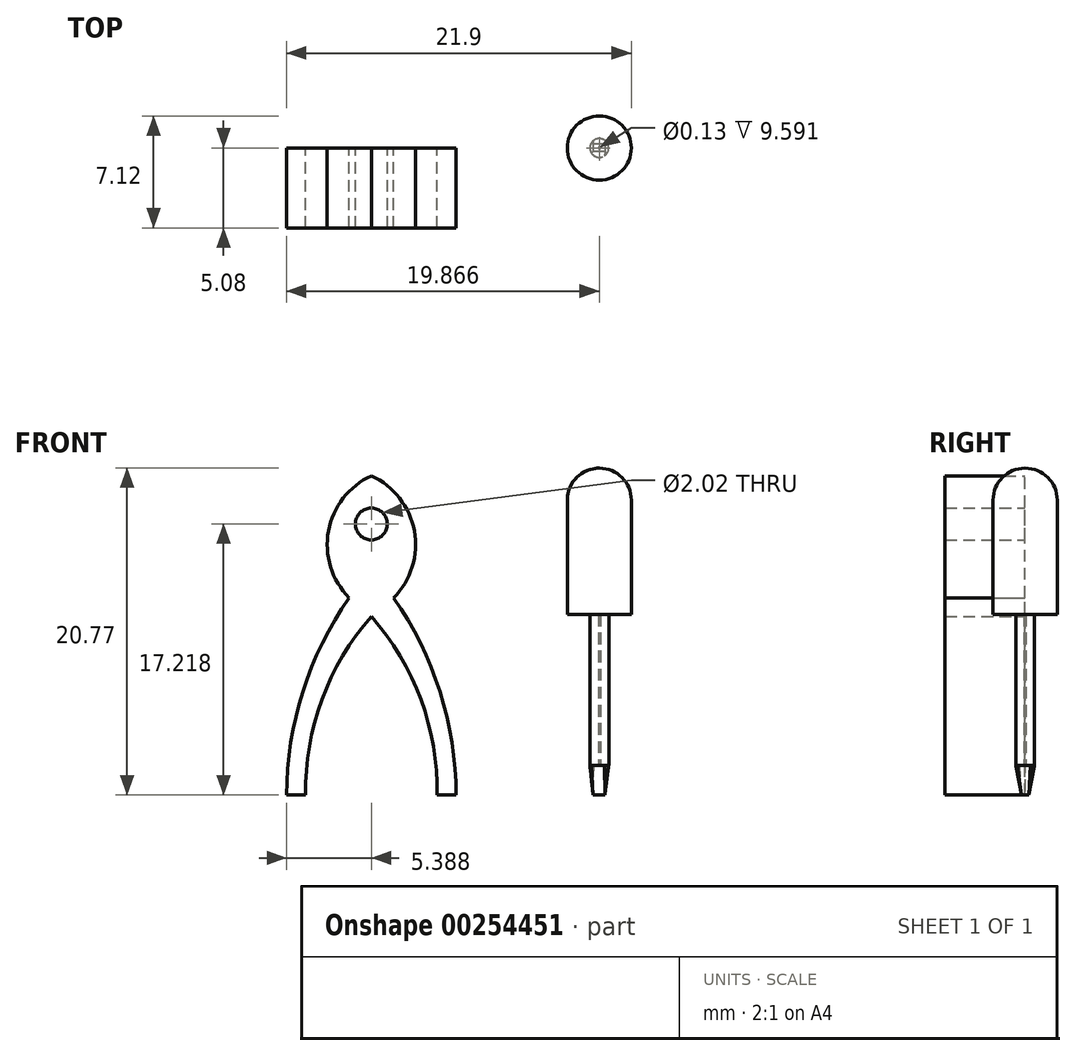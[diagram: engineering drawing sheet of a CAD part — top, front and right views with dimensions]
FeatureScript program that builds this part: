
annotation { "Feature Type Name" : "Feature", "Feature Type Description" : "" }
export const myFeature = defineFeature(function(context is Context, id is Id, definition is map)
    precondition{}
    {
        {
            var Q0;
            Q0=qCreatedBy(makeId("Front.planeOp"),FACE);
            var sketch = newSketch(context, id + "F0", { "sketchPlane" : qUnion([Q0])});
            skArc(sketch, "E0", {"start": v(5.39, 14.35) * mm, "mid": v(1.41, 7.66) * mm, "end": v(0, 0) * mm});
            skLineSegment(sketch, "E1", {"start": v(0, 0) * mm, "end": v(1.21, 0) * mm});
            skLineSegment(sketch, "E2", {"start": v(5.39, 14.35) * mm, "end": v(5.39, 11.35) * mm});
            skArc(sketch, "E3", {"start": v(5.39, 11.35) * mm, "mid": v(2.25, 6.06) * mm, "end": v(1.21, 0) * mm});
            skArc(sketch, "E4.MirrorCS", {"start": v(5.39, 14.35) * mm, "mid": v(9.37, 7.66) * mm, "end": v(10.78, 0) * mm});
            skArc(sketch, "E5.MirrorCS", {"start": v(5.39, 11.35) * mm, "mid": v(8.53, 6.06) * mm, "end": v(9.57, 0) * mm});
            skLineSegment(sketch, "E6.MirrorCS", {"start": v(10.78, 0) * mm, "end": v(9.57, 0) * mm});
            skArc(sketch, "E7", {"start": v(5.39, 20.28) * mm, "mid": v(2.66, 16.77) * mm, "end": v(3.97, 12.53) * mm});
            skLineSegment(sketch, "E8", {"start": v(5.39, 20.28) * mm, "end": v(5.39, 18.23) * mm});
            skLineSegment(sketch, "E9", {"start": v(5.39, 14.35) * mm, "end": v(5.39, 16.2) * mm});
            skArc(sketch, "E10", {"start": v(5.39, 18.23) * mm, "mid": v(4.38, 17.22) * mm, "end": v(5.39, 16.2) * mm});
            skArc(sketch, "E11.MirrorCS", {"start": v(5.39, 18.23) * mm, "mid": v(6.4, 17.22) * mm, "end": v(5.39, 16.2) * mm});
            skArc(sketch, "E12.MirrorCS", {"start": v(5.39, 20.28) * mm, "mid": v(8.11, 16.77) * mm, "end": v(6.8, 12.53) * mm});
            skSolve(sketch);
        }
        {
            var Q0;
            Q0=qSketchRegion(id+"F0",true);
            extrude(context, id + "F1", {"entities" : qUnion([Q0]), "depth" : 5.08 * mm});
        }
        {
            var Q0;
            Q0=qCreatedBy(makeId("Front.planeOp"),FACE);
            var sketch = newSketch(context, id + "F2", { "sketchPlane" : qUnion([Q0])});
            skLineSegment(sketch, "E13", {"start": v(17.83, 18.73) * mm, "end": v(17.83, 11.47) * mm});
            skLineSegment(sketch, "E14", {"start": v(17.83, 11.47) * mm, "end": v(19.87, 11.47) * mm});
            skLineSegment(sketch, "E15", {"start": v(19.87, 11.47) * mm, "end": v(19.87, 18.73) * mm});
            skPoint(sketch, "E16.middle", {"position": v(18.85, 11.47) * mm});
            skLineSegment(sketch, "E17.bottom", {"start": v(19.27, 11.47) * mm, "end": v(19.8, 11.47) * mm});
            skLineSegment(sketch, "E17.top", {"start": v(19.27, 1.88) * mm, "end": v(19.8, 1.88) * mm});
            skLineSegment(sketch, "E17.left", {"start": v(19.27, 11.47) * mm, "end": v(19.27, 1.88) * mm});
            skLineSegment(sketch, "E17.right", {"start": v(19.8, 11.47) * mm, "end": v(19.8, 1.88) * mm});
            skArc(sketch, "E18", {"start": v(19.87, 20.77) * mm, "mid": v(18.43, 20.17) * mm, "end": v(17.83, 18.73) * mm});
            skLineSegment(sketch, "E19", {"start": v(19.87, 18.73) * mm, "end": v(19.87, 20.77) * mm});
            skSolve(sketch);
        }
        {
            var Q0;
            Q0 = qSketchRegion(id + "F2", true);
            var Q1;
            Q1=sQuery(id+"F2.wireOp",EDGE,"E15");
            revolve(context, id + "F3", {"entities" : qUnion([Q0]), "axis" : qUnion([Q1]), "revolveType" : RevolveType.FULL});
        }
        {
            var Q0;
            Q0=qCreatedBy(makeId("Top.planeOp"),FACE);
            var sketch = newSketch(context, id + "F4", { "sketchPlane" : qUnion([Q0])});
            skLineSegment(sketch, "E20.bottom", {"start": v(20.21, 0.23) * mm, "end": v(19.47, 0.23) * mm});
            skLineSegment(sketch, "E20.top", {"start": v(20.21, -0.23) * mm, "end": v(19.47, -0.23) * mm});
            skLineSegment(sketch, "E20.left", {"start": v(20.21, 0.23) * mm, "end": v(20.21, -0.23) * mm});
            skLineSegment(sketch, "E20.right", {"start": v(19.47, 0.23) * mm, "end": v(19.47, -0.23) * mm});
            skPoint(sketch, "E20.middle", {"position": v(19.84, 0) * mm});
            skSolve(sketch);
        }
        {
            var Q0;
            Q0=makeQuery(id+"F3.opRevolve","SWEPT_FACE",FACE,{"disambiguationData":[OSD([sQuery(id+"F2.wireOp",EDGE,"E17.top")])]});
            var sketch = newSketch(context, id + "F5", { "sketchPlane" : qUnion([Q0])});
            skCircle(sketch, "E21", {"center": v(19.87, 0) * mm, "radius": 0.6 * mm});
            skPoint(sketch, "E21.first.point", {"position": v(19.27, 0) * mm});
            skPoint(sketch, "E21.second.point", {"position": v(19.92, 0.6) * mm});
            skPoint(sketch, "E21.third.point", {"position": v(20.37, -0.32) * mm});
            skSolve(sketch);
        }
        {
            var Q1;
            Q1=makeQuery(id+"F4.imprint","IMPRINT",FACE,{"disambiguationData":[TD([[makeQuery(id+"F4.imprint","IMPRINT",EDGE,{"derivedFrom":sQuery(id+"F4.wireOp",EDGE,"E20.bottom")}),1.0]])]});
            var Q2;
            Q2 = qSketchRegion(id + "F5", true);
            loft(context, id + "F6", {"operationType" : NewBodyOperationType.ADD, "sheetProfilesArray" : [{ "sheetProfileEntities" : qUnion([Q1]) }, { "sheetProfileEntities" : qUnion([Q2]) }]});
        }
    });
